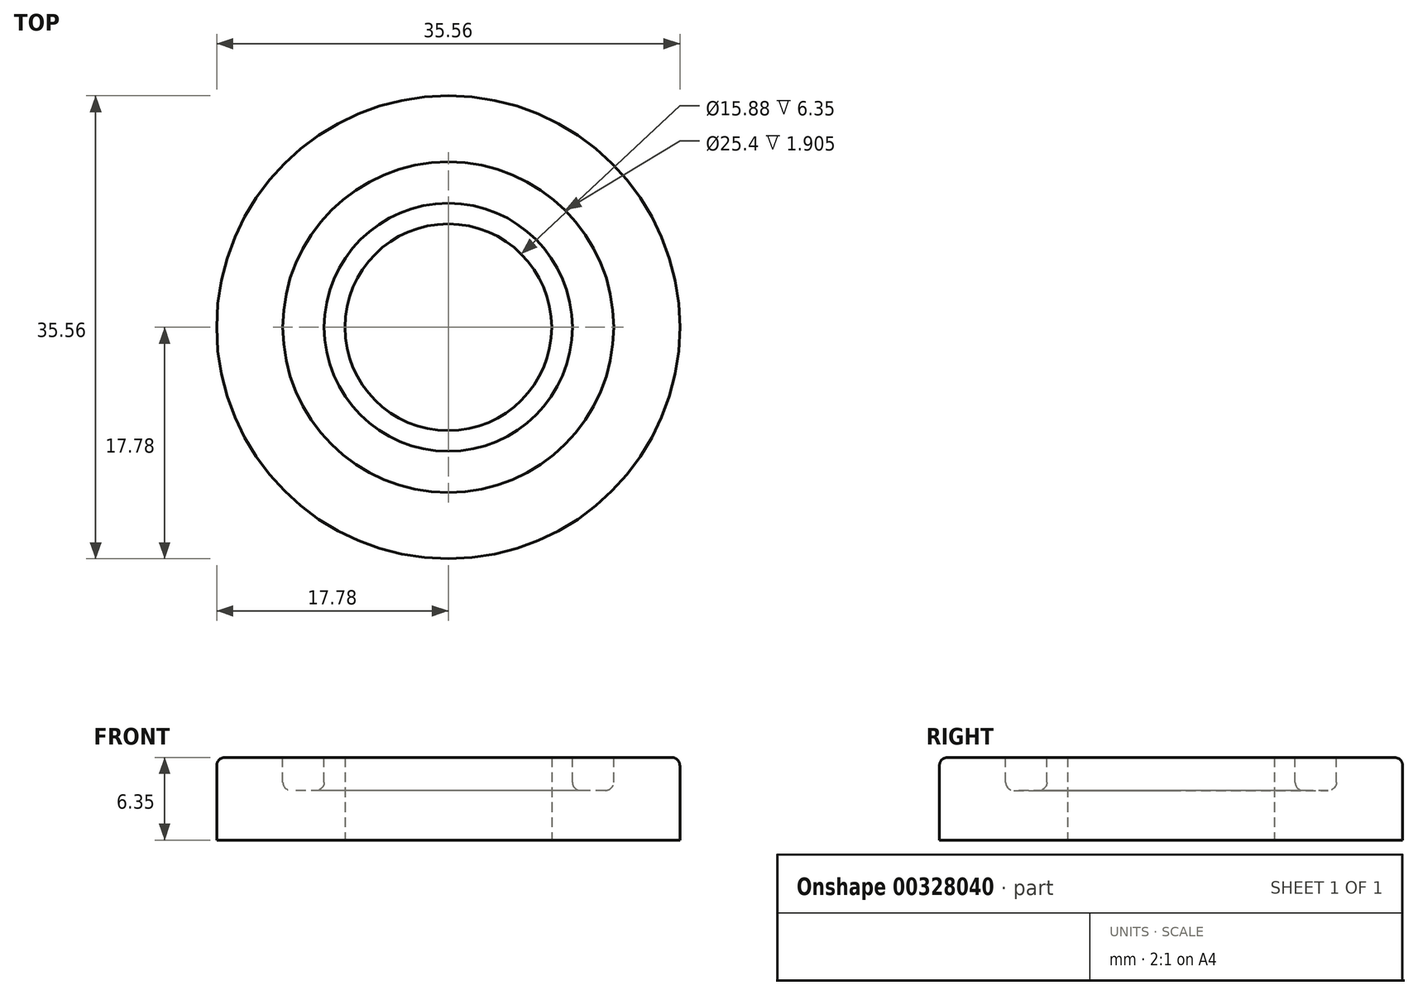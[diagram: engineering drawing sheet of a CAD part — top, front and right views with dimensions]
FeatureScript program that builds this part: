
annotation { "Feature Type Name" : "Feature", "Feature Type Description" : "" }
export const myFeature = defineFeature(function(context is Context, id is Id, definition is map)
    precondition{}
    {
        {
            var Q0;
            Q0=qCreatedBy(makeId("Top.planeOp"),FACE);
            var sketch = newSketch(context, id + "F0", { "sketchPlane" : qUnion([Q0])});
            skCircle(sketch, "E0", {"center": v(0, 0) * mm, "radius": 7.94 * mm});
            skCircle(sketch, "E1", {"center": v(0, 0) * mm, "radius": 17.78 * mm});
            skSolve(sketch);
        }
        {
            var Q0;
            Q0 = qSketchRegion(id + "F0", true);
            extrude(context, id + "F1", {"entities" : qUnion([Q0]), "depth" : 6.35 * mm});
        }
        {
            var Q0;
            Q0=makeQuery(id+"F1.opExtrude","CAP_FACE",FACE,{"disambiguationData":[OSD([sQuery(id+"F0.wireOp",EDGE,"E0"),sQuery(id+"F0.wireOp",EDGE,"E1")])],"isStart":false});
            var sketch = newSketch(context, id + "F2", { "sketchPlane" : qUnion([Q0])});
            skCircle(sketch, "E2", {"center": v(0, 0) * mm, "radius": 9.53 * mm});
            skCircle(sketch, "E3", {"center": v(0, 0) * mm, "radius": 12.7 * mm});
            skSolve(sketch);
        }
        {
            var Q0;
            Q0 = qSketchRegion(id + "F2", true);
            extrude(context, id + "F3", {"entities" : qUnion([Q0]), "operationType" : NewBodyOperationType.REMOVE, "oppositeDirection" : true, "depth" : 2.54 * mm});
        }
        {
            var Q0;
            Q0=makeQuery(id+"F1.opExtrude","CAP_EDGE",EDGE,{"disambiguationData":[OSD([sQuery(id+"F0.wireOp",EDGE,"E1")])],"isStart":false});
            var Q1;
            Q1=makeQuery(id+"F3.boolean.opBoolean","COPY",EDGE,{"derivedFrom":makeQuery(id+"F3.opExtrude","CAP_EDGE",EDGE,{"disambiguationData":[OSD([sQuery(id+"F2.wireOp",EDGE,"E3")])],"isStart":false})});
            var Q2;
            Q2=makeQuery(id+"F3.boolean.opBoolean","COPY",EDGE,{"derivedFrom":makeQuery(id+"F3.opExtrude","CAP_EDGE",EDGE,{"disambiguationData":[OSD([sQuery(id+"F2.wireOp",EDGE,"E2")])],"isStart":false})});
            fillet(context, id + "F4", {"entities" : qUnion([Q0, Q1, Q2]), "radius" : 0.64 * mm, "tangentPropagation" : true, "allowEdgeOverflow" : false});
        }
    });
